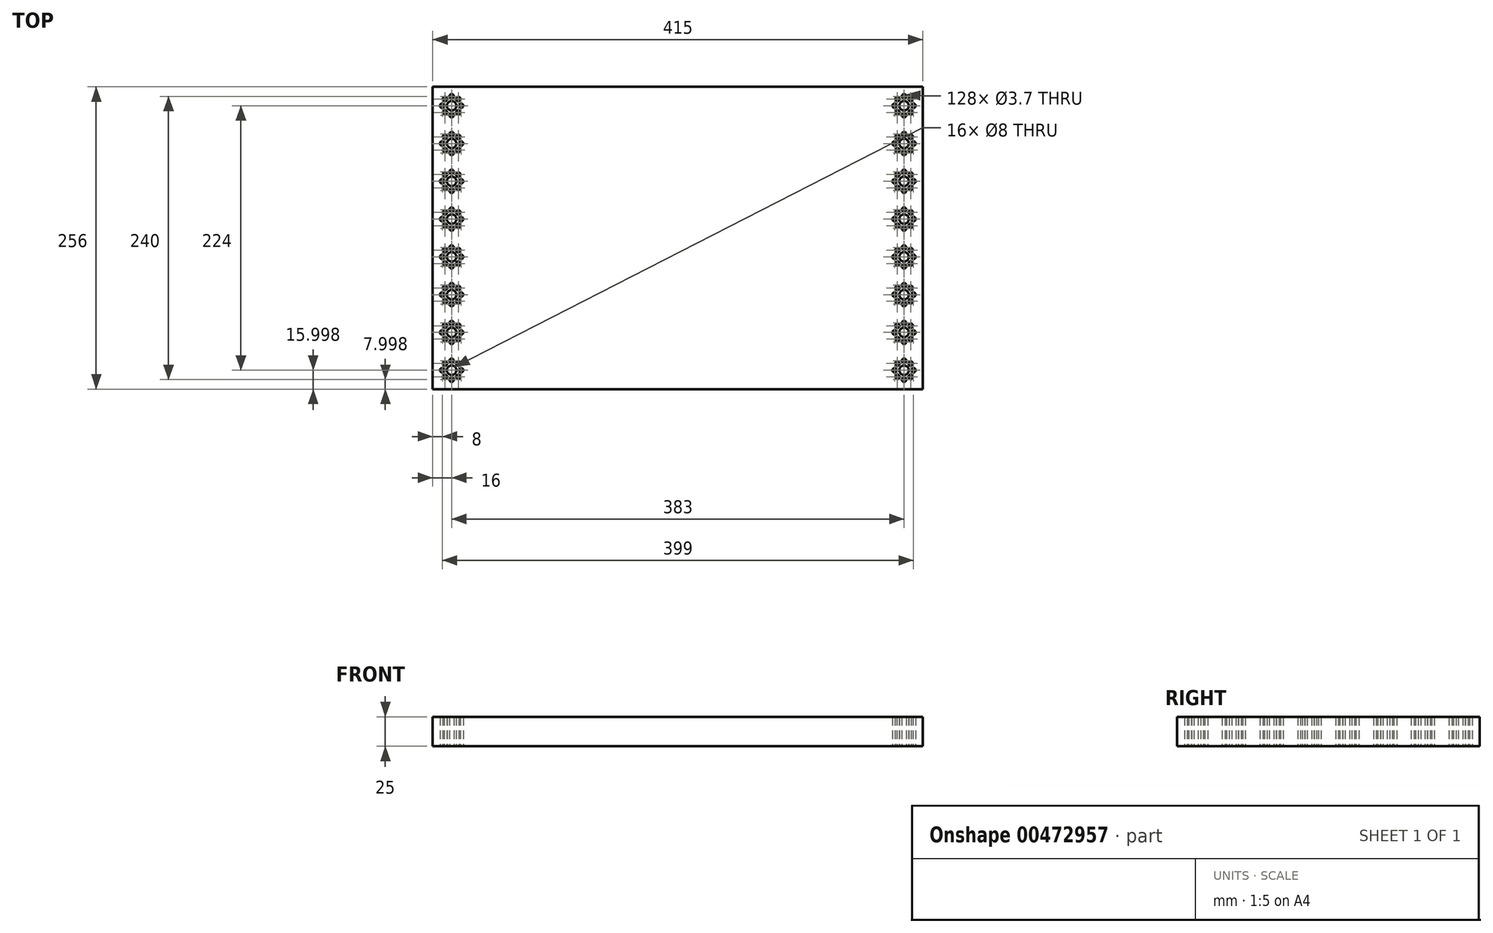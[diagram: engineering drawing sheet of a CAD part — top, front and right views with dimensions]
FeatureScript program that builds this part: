
annotation { "Feature Type Name" : "Feature", "Feature Type Description" : "" }
export const myFeature = defineFeature(function(context is Context, id is Id, definition is map)
    precondition{}
    {
        {
            var Q0;
            Q0=qCreatedBy(makeId("Top.planeOp"),FACE);
            var sketch = newSketch(context, id + "F0", { "sketchPlane" : qUnion([Q0])});
            skLineSegment(sketch, "E0.bottom", {"start": v(-328.23, 187.1) * mm, "end": v(86.77, 187.1) * mm});
            skLineSegment(sketch, "E0.top", {"start": v(-328.23, -68.9) * mm, "end": v(86.77, -68.9) * mm});
            skLineSegment(sketch, "E0.left", {"start": v(-328.23, 187.1) * mm, "end": v(-328.23, -68.9) * mm});
            skLineSegment(sketch, "E0.right", {"start": v(86.77, 187.1) * mm, "end": v(86.77, -68.9) * mm});
            skCircle(sketch, "E1", {"center": v(-312.23, 179.1) * mm, "radius": 1.85 * mm});
            skCircle(sketch, "E2", {"center": v(-312.23, 171.1) * mm, "radius": 4 * mm});
            skCircle(sketch, "E3.1.0", {"center": v(-317.89, 176.77) * mm, "radius": 1.85 * mm});
            skCircle(sketch, "E3.2.0", {"center": v(-320.23, 171.1) * mm, "radius": 1.85 * mm});
            skCircle(sketch, "E4.1.3.0", {"center": v(-317.89, 165.45) * mm, "radius": 1.85 * mm});
            skCircle(sketch, "E4.1.4.0", {"center": v(-312.23, 163.1) * mm, "radius": 1.85 * mm});
            skCircle(sketch, "E4.1.5.0", {"center": v(-306.57, 165.45) * mm, "radius": 1.85 * mm});
            skCircle(sketch, "E4.1.6.0", {"center": v(-304.23, 171.1) * mm, "radius": 1.85 * mm});
            skCircle(sketch, "E4.1.7.0", {"center": v(-306.57, 176.77) * mm, "radius": 1.85 * mm});
            skCircle(sketch, "E5.0.1.0", {"center": v(-306.57, 144.77) * mm, "radius": 1.85 * mm});
            skPoint(sketch, "E5.0.1.1", {"position": v(-312.23, 139.1) * mm});
            skCircle(sketch, "E5.0.1.2", {"center": v(-304.23, 139.1) * mm, "radius": 1.85 * mm});
            skCircle(sketch, "E5.0.1.3", {"center": v(-306.57, 133.45) * mm, "radius": 1.85 * mm});
            skCircle(sketch, "E5.0.1.4", {"center": v(-312.23, 131.1) * mm, "radius": 1.85 * mm});
            skCircle(sketch, "E5.0.1.5", {"center": v(-317.89, 133.45) * mm, "radius": 1.85 * mm});
            skCircle(sketch, "E5.0.1.6", {"center": v(-320.23, 139.1) * mm, "radius": 1.85 * mm});
            skCircle(sketch, "E5.0.1.7", {"center": v(-317.89, 144.77) * mm, "radius": 1.85 * mm});
            skCircle(sketch, "E5.0.1.8", {"center": v(-312.23, 139.1) * mm, "radius": 4 * mm});
            skCircle(sketch, "E5.0.1.9", {"center": v(-312.23, 147.1) * mm, "radius": 1.85 * mm});
            skCircle(sketch, "E5.0.2.0", {"center": v(-306.57, 112.77) * mm, "radius": 1.85 * mm});
            skPoint(sketch, "E5.0.2.1", {"position": v(-312.23, 107.1) * mm});
            skCircle(sketch, "E5.0.2.2", {"center": v(-304.23, 107.1) * mm, "radius": 1.85 * mm});
            skCircle(sketch, "E5.0.2.3", {"center": v(-306.57, 101.45) * mm, "radius": 1.85 * mm});
            skCircle(sketch, "E5.0.2.4", {"center": v(-312.23, 99.1) * mm, "radius": 1.85 * mm});
            skCircle(sketch, "E5.0.2.5", {"center": v(-317.89, 101.45) * mm, "radius": 1.85 * mm});
            skCircle(sketch, "E5.0.2.6", {"center": v(-320.23, 107.1) * mm, "radius": 1.85 * mm});
            skCircle(sketch, "E5.0.2.7", {"center": v(-317.89, 112.77) * mm, "radius": 1.85 * mm});
            skCircle(sketch, "E5.0.2.8", {"center": v(-312.23, 107.1) * mm, "radius": 4 * mm});
            skCircle(sketch, "E5.0.2.9", {"center": v(-312.23, 115.1) * mm, "radius": 1.85 * mm});
            skCircle(sketch, "E5.0.3.0", {"center": v(-306.57, 80.77) * mm, "radius": 1.85 * mm});
            skPoint(sketch, "E5.0.3.1", {"position": v(-312.23, 75.1) * mm});
            skCircle(sketch, "E5.0.3.2", {"center": v(-304.23, 75.1) * mm, "radius": 1.85 * mm});
            skCircle(sketch, "E5.0.3.3", {"center": v(-306.57, 69.45) * mm, "radius": 1.85 * mm});
            skCircle(sketch, "E5.0.3.4", {"center": v(-312.23, 67.1) * mm, "radius": 1.85 * mm});
            skCircle(sketch, "E5.0.3.5", {"center": v(-317.89, 69.45) * mm, "radius": 1.85 * mm});
            skCircle(sketch, "E5.0.3.6", {"center": v(-320.23, 75.1) * mm, "radius": 1.85 * mm});
            skCircle(sketch, "E5.0.3.7", {"center": v(-317.89, 80.77) * mm, "radius": 1.85 * mm});
            skCircle(sketch, "E5.0.3.8", {"center": v(-312.23, 75.1) * mm, "radius": 4 * mm});
            skCircle(sketch, "E5.0.3.9", {"center": v(-312.23, 83.1) * mm, "radius": 1.85 * mm});
            skCircle(sketch, "E5.0.4.0", {"center": v(-306.57, 48.77) * mm, "radius": 1.85 * mm});
            skPoint(sketch, "E5.0.4.1", {"position": v(-312.23, 43.1) * mm});
            skCircle(sketch, "E5.0.4.2", {"center": v(-304.23, 43.1) * mm, "radius": 1.85 * mm});
            skCircle(sketch, "E5.0.4.3", {"center": v(-306.57, 37.45) * mm, "radius": 1.85 * mm});
            skCircle(sketch, "E5.0.4.4", {"center": v(-312.23, 35.1) * mm, "radius": 1.85 * mm});
            skCircle(sketch, "E5.0.4.5", {"center": v(-317.89, 37.45) * mm, "radius": 1.85 * mm});
            skCircle(sketch, "E5.0.4.6", {"center": v(-320.23, 43.1) * mm, "radius": 1.85 * mm});
            skCircle(sketch, "E5.0.4.7", {"center": v(-317.89, 48.77) * mm, "radius": 1.85 * mm});
            skCircle(sketch, "E5.0.4.8", {"center": v(-312.23, 43.1) * mm, "radius": 4 * mm});
            skCircle(sketch, "E5.0.4.9", {"center": v(-312.23, 51.1) * mm, "radius": 1.85 * mm});
            skCircle(sketch, "E5.0.5.0", {"center": v(-306.57, 16.77) * mm, "radius": 1.85 * mm});
            skPoint(sketch, "E5.0.5.1", {"position": v(-312.23, 11.1) * mm});
            skCircle(sketch, "E5.0.5.2", {"center": v(-304.23, 11.1) * mm, "radius": 1.85 * mm});
            skCircle(sketch, "E5.0.5.3", {"center": v(-306.57, 5.45) * mm, "radius": 1.85 * mm});
            skCircle(sketch, "E5.0.5.4", {"center": v(-312.23, 3.1) * mm, "radius": 1.85 * mm});
            skCircle(sketch, "E5.0.5.5", {"center": v(-317.89, 5.45) * mm, "radius": 1.85 * mm});
            skCircle(sketch, "E5.0.5.6", {"center": v(-320.23, 11.1) * mm, "radius": 1.85 * mm});
            skCircle(sketch, "E5.0.5.7", {"center": v(-317.89, 16.77) * mm, "radius": 1.85 * mm});
            skCircle(sketch, "E5.0.5.8", {"center": v(-312.23, 11.1) * mm, "radius": 4 * mm});
            skCircle(sketch, "E5.0.5.9", {"center": v(-312.23, 19.1) * mm, "radius": 1.85 * mm});
            skCircle(sketch, "E5.0.6.0", {"center": v(-306.57, -15.23) * mm, "radius": 1.85 * mm});
            skPoint(sketch, "E5.0.6.1", {"position": v(-312.23, -20.9) * mm});
            skCircle(sketch, "E5.0.6.2", {"center": v(-304.23, -20.9) * mm, "radius": 1.85 * mm});
            skCircle(sketch, "E5.0.6.3", {"center": v(-306.57, -26.55) * mm, "radius": 1.85 * mm});
            skCircle(sketch, "E5.0.6.4", {"center": v(-312.23, -28.9) * mm, "radius": 1.85 * mm});
            skCircle(sketch, "E5.0.6.5", {"center": v(-317.89, -26.55) * mm, "radius": 1.85 * mm});
            skCircle(sketch, "E5.0.6.6", {"center": v(-320.23, -20.9) * mm, "radius": 1.85 * mm});
            skCircle(sketch, "E5.0.6.7", {"center": v(-317.89, -15.23) * mm, "radius": 1.85 * mm});
            skCircle(sketch, "E5.0.6.8", {"center": v(-312.23, -20.9) * mm, "radius": 4 * mm});
            skCircle(sketch, "E5.0.6.9", {"center": v(-312.23, -12.9) * mm, "radius": 1.85 * mm});
            skCircle(sketch, "E5.0.7.0", {"center": v(-306.57, -47.23) * mm, "radius": 1.85 * mm});
            skPoint(sketch, "E5.0.7.1", {"position": v(-312.23, -52.9) * mm});
            skCircle(sketch, "E5.0.7.2", {"center": v(-304.23, -52.9) * mm, "radius": 1.85 * mm});
            skCircle(sketch, "E5.0.7.3", {"center": v(-306.57, -58.55) * mm, "radius": 1.85 * mm});
            skCircle(sketch, "E5.0.7.4", {"center": v(-312.23, -60.9) * mm, "radius": 1.85 * mm});
            skCircle(sketch, "E5.0.7.5", {"center": v(-317.89, -58.55) * mm, "radius": 1.85 * mm});
            skCircle(sketch, "E5.0.7.6", {"center": v(-320.23, -52.9) * mm, "radius": 1.85 * mm});
            skCircle(sketch, "E5.0.7.7", {"center": v(-317.89, -47.23) * mm, "radius": 1.85 * mm});
            skCircle(sketch, "E5.0.7.8", {"center": v(-312.23, -52.9) * mm, "radius": 4 * mm});
            skCircle(sketch, "E5.0.7.9", {"center": v(-312.23, -44.9) * mm, "radius": 1.85 * mm});
            skLineSegment(sketch, "E5.direction1", {"start": v(-317.89, 165.45) * mm, "end": v(-292.89, 165.45) * mm, "construction": true});
            skLineSegment(sketch, "E5.direction2", {"start": v(-317.89, 165.45) * mm, "end": v(-317.89, 133.45) * mm, "construction": true});
            skLineSegment(sketch, "E6", {"start": v(-120.73, -68.9) * mm, "end": v(-120.73, 187.1) * mm, "construction": true});
            skCircle(sketch, "E7.MirrorC", {"center": v(78.77, 171.1) * mm, "radius": 1.85 * mm});
            skCircle(sketch, "E8.MirrorC", {"center": v(76.43, 165.45) * mm, "radius": 1.85 * mm});
            skCircle(sketch, "E9.MirrorC", {"center": v(78.77, 139.1) * mm, "radius": 1.85 * mm});
            skCircle(sketch, "E10.MirrorC", {"center": v(76.43, 133.45) * mm, "radius": 1.85 * mm});
            skCircle(sketch, "E11.MirrorC", {"center": v(65.11, -15.23) * mm, "radius": 1.85 * mm});
            skCircle(sketch, "E12.MirrorC", {"center": v(76.43, 101.45) * mm, "radius": 1.85 * mm});
            skCircle(sketch, "E13.MirrorC", {"center": v(70.77, -52.9) * mm, "radius": 4 * mm});
            skCircle(sketch, "E14.MirrorC", {"center": v(76.43, 144.77) * mm, "radius": 1.85 * mm});
            skCircle(sketch, "E15.MirrorC", {"center": v(78.77, 107.1) * mm, "radius": 1.85 * mm});
            skCircle(sketch, "E16.MirrorC", {"center": v(70.77, -44.9) * mm, "radius": 1.85 * mm});
            skCircle(sketch, "E17.MirrorC", {"center": v(70.77, 139.1) * mm, "radius": 4 * mm});
            skCircle(sketch, "E18.MirrorC", {"center": v(78.77, 43.1) * mm, "radius": 1.85 * mm});
            skCircle(sketch, "E19.MirrorC", {"center": v(78.77, 75.1) * mm, "radius": 1.85 * mm});
            skCircle(sketch, "E20.MirrorC", {"center": v(70.77, 107.1) * mm, "radius": 4 * mm});
            skCircle(sketch, "E21.MirrorC", {"center": v(76.43, 112.77) * mm, "radius": 1.85 * mm});
            skCircle(sketch, "E22.MirrorC", {"center": v(76.43, -26.55) * mm, "radius": 1.85 * mm});
            skCircle(sketch, "E23.MirrorC", {"center": v(76.43, 5.45) * mm, "radius": 1.85 * mm});
            skCircle(sketch, "E24.MirrorC", {"center": v(76.43, 48.77) * mm, "radius": 1.85 * mm});
            skCircle(sketch, "E25.MirrorC", {"center": v(70.77, 115.1) * mm, "radius": 1.85 * mm});
            skCircle(sketch, "E26.MirrorC", {"center": v(76.43, 80.77) * mm, "radius": 1.85 * mm});
            skCircle(sketch, "E27.MirrorC", {"center": v(78.77, -20.9) * mm, "radius": 1.85 * mm});
            skCircle(sketch, "E28.MirrorC", {"center": v(70.77, -60.9) * mm, "radius": 1.85 * mm});
            skCircle(sketch, "E29.MirrorC", {"center": v(70.77, 43.1) * mm, "radius": 4 * mm});
            skCircle(sketch, "E30.MirrorC", {"center": v(78.77, 11.1) * mm, "radius": 1.85 * mm});
            skCircle(sketch, "E31.MirrorC", {"center": v(70.77, 75.1) * mm, "radius": 4 * mm});
            skCircle(sketch, "E32.MirrorC", {"center": v(65.11, 144.77) * mm, "radius": 1.85 * mm});
            skCircle(sketch, "E33.MirrorC", {"center": v(70.77, 179.1) * mm, "radius": 1.85 * mm});
            skCircle(sketch, "E34.MirrorC", {"center": v(70.77, 171.1) * mm, "radius": 4 * mm});
            skCircle(sketch, "E35.MirrorC", {"center": v(76.43, 176.77) * mm, "radius": 1.85 * mm});
            skCircle(sketch, "E36.MirrorC", {"center": v(70.77, 163.1) * mm, "radius": 1.85 * mm});
            skCircle(sketch, "E37.MirrorC", {"center": v(65.11, 165.45) * mm, "radius": 1.85 * mm});
            skCircle(sketch, "E38.MirrorC", {"center": v(65.11, 176.77) * mm, "radius": 1.85 * mm});
            skCircle(sketch, "E39.MirrorC", {"center": v(76.43, -58.55) * mm, "radius": 1.85 * mm});
            skCircle(sketch, "E40.MirrorC", {"center": v(76.43, -15.23) * mm, "radius": 1.85 * mm});
            skCircle(sketch, "E41.MirrorC", {"center": v(70.77, 51.1) * mm, "radius": 1.85 * mm});
            skCircle(sketch, "E42.MirrorC", {"center": v(70.77, 11.1) * mm, "radius": 4 * mm});
            skCircle(sketch, "E43.MirrorC", {"center": v(78.77, -52.9) * mm, "radius": 1.85 * mm});
            skCircle(sketch, "E44.MirrorC", {"center": v(70.77, -20.9) * mm, "radius": 4 * mm});
            skCircle(sketch, "E45.MirrorC", {"center": v(76.43, -47.23) * mm, "radius": 1.85 * mm});
            skCircle(sketch, "E46.MirrorC", {"center": v(65.11, 37.45) * mm, "radius": 1.85 * mm});
            skCircle(sketch, "E47.MirrorC", {"center": v(65.11, -47.23) * mm, "radius": 1.85 * mm});
            skCircle(sketch, "E48.MirrorC", {"center": v(65.11, 5.45) * mm, "radius": 1.85 * mm});
            skCircle(sketch, "E49.MirrorC", {"center": v(76.43, 69.45) * mm, "radius": 1.85 * mm});
            skCircle(sketch, "E50.MirrorC", {"center": v(62.77, -20.9) * mm, "radius": 1.85 * mm});
            skCircle(sketch, "E51.MirrorC", {"center": v(70.77, 35.1) * mm, "radius": 1.85 * mm});
            skLineSegment(sketch, "E52.MirrorCS", {"start": v(76.43, 165.45) * mm, "end": v(76.43, 133.45) * mm, "construction": true});
            skCircle(sketch, "E53.MirrorC", {"center": v(62.77, -52.9) * mm, "radius": 1.85 * mm});
            skCircle(sketch, "E54.MirrorC", {"center": v(70.77, -28.9) * mm, "radius": 1.85 * mm});
            skCircle(sketch, "E55.MirrorC", {"center": v(70.77, 3.1) * mm, "radius": 1.85 * mm});
            skCircle(sketch, "E56.MirrorC", {"center": v(65.11, -26.55) * mm, "radius": 1.85 * mm});
            skCircle(sketch, "E57.MirrorC", {"center": v(76.43, 37.45) * mm, "radius": 1.85 * mm});
            skLineSegment(sketch, "E58.MirrorCS", {"start": v(76.43, 165.45) * mm, "end": v(51.43, 165.45) * mm, "construction": true});
            skCircle(sketch, "E59.MirrorC", {"center": v(70.77, 147.1) * mm, "radius": 1.85 * mm});
            skCircle(sketch, "E60.MirrorC", {"center": v(65.11, -58.55) * mm, "radius": 1.85 * mm});
            skCircle(sketch, "E61.MirrorC", {"center": v(65.11, 112.77) * mm, "radius": 1.85 * mm});
            skCircle(sketch, "E62.MirrorC", {"center": v(65.11, 80.77) * mm, "radius": 1.85 * mm});
            skCircle(sketch, "E63.MirrorC", {"center": v(62.77, 139.1) * mm, "radius": 1.85 * mm});
            skCircle(sketch, "E64.MirrorC", {"center": v(65.11, 133.45) * mm, "radius": 1.85 * mm});
            skCircle(sketch, "E65.MirrorC", {"center": v(62.77, 171.1) * mm, "radius": 1.85 * mm});
            skCircle(sketch, "E66.MirrorC", {"center": v(76.43, 16.77) * mm, "radius": 1.85 * mm});
            skCircle(sketch, "E67.MirrorC", {"center": v(70.77, 83.1) * mm, "radius": 1.85 * mm});
            skCircle(sketch, "E68.MirrorC", {"center": v(62.77, 107.1) * mm, "radius": 1.85 * mm});
            skCircle(sketch, "E69.MirrorC", {"center": v(70.77, 131.1) * mm, "radius": 1.85 * mm});
            skCircle(sketch, "E70.MirrorC", {"center": v(62.77, 75.1) * mm, "radius": 1.85 * mm});
            skCircle(sketch, "E71.MirrorC", {"center": v(65.11, 48.77) * mm, "radius": 1.85 * mm});
            skCircle(sketch, "E72.MirrorC", {"center": v(65.11, 101.45) * mm, "radius": 1.85 * mm});
            skCircle(sketch, "E73.MirrorC", {"center": v(65.11, 16.77) * mm, "radius": 1.85 * mm});
            skCircle(sketch, "E74.MirrorC", {"center": v(65.11, 69.45) * mm, "radius": 1.85 * mm});
            skCircle(sketch, "E75.MirrorC", {"center": v(70.77, 19.1) * mm, "radius": 1.85 * mm});
            skCircle(sketch, "E76.MirrorC", {"center": v(62.77, 43.1) * mm, "radius": 1.85 * mm});
            skCircle(sketch, "E77.MirrorC", {"center": v(70.77, 99.1) * mm, "radius": 1.85 * mm});
            skCircle(sketch, "E78.MirrorC", {"center": v(70.77, -12.9) * mm, "radius": 1.85 * mm});
            skCircle(sketch, "E79.MirrorC", {"center": v(62.77, 11.1) * mm, "radius": 1.85 * mm});
            skCircle(sketch, "E80.MirrorC", {"center": v(70.77, 67.1) * mm, "radius": 1.85 * mm});
            skSolve(sketch);
        }
        {
            var Q0;
            Q0=makeQuery(id+"F0.imprint","IMPRINT",FACE,{"disambiguationData":[TD([[makeQuery(id+"F0.imprint","IMPRINT",EDGE,{"derivedFrom":sQuery(id+"F0.wireOp",EDGE,"E0.bottom")}),-1.0]])]});
            extrude(context, id + "F1", {"entities" : qUnion([Q0]), "depth" : 25 * mm});
        }
    });
